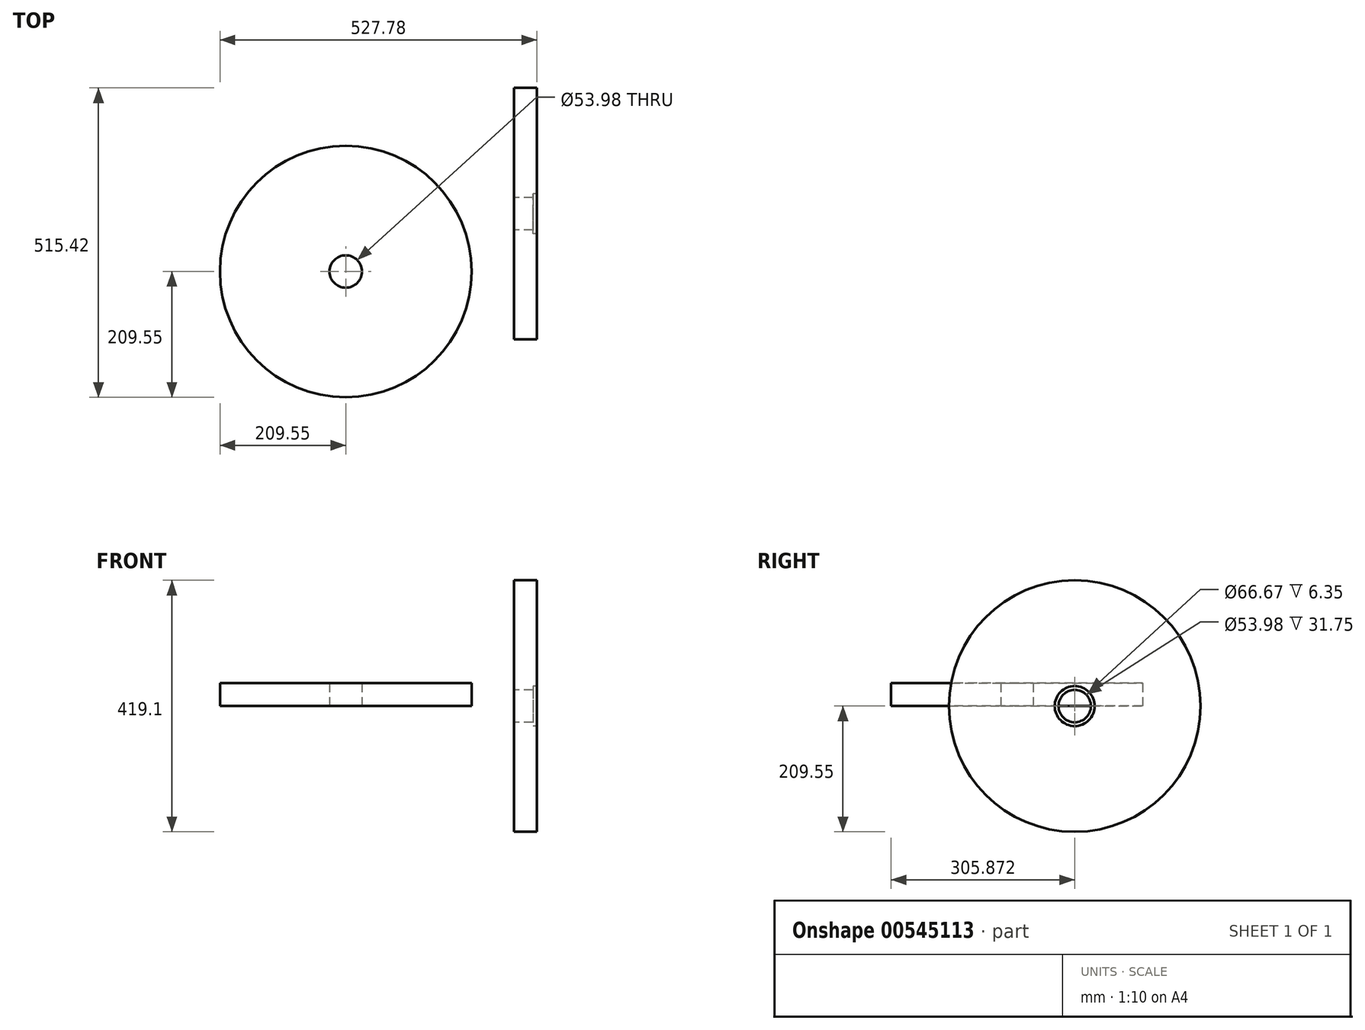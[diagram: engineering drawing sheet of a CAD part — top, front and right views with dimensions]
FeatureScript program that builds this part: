
annotation { "Feature Type Name" : "Feature", "Feature Type Description" : "" }
export const myFeature = defineFeature(function(context is Context, id is Id, definition is map)
    precondition{}
    {
        {
            var Q0;
            Q0=qCreatedBy(makeId("Top.planeOp"),FACE);
            var sketch = newSketch(context, id + "F0", { "sketchPlane" : qUnion([Q0])});
            skCircle(sketch, "E0", {"center": v(0, 0) * mm, "radius": 209.55 * mm});
            skCircle(sketch, "E1", {"center": v(0, 0) * mm, "radius": 26.99 * mm});
            skSolve(sketch);
        }
        {
            var Q0;
            Q0=makeQuery(id+"F0.imprint","IMPRINT",FACE,{"disambiguationData":[TD([[makeQuery(id+"F0.imprint","IMPRINT",EDGE,{"derivedFrom":sQuery(id+"F0.wireOp",EDGE,"E0")}),1.0]])]});
            extrude(context, id + "F1", {"entities" : qUnion([Q0]), "depth" : 38.1 * mm, "offsetDistance" : 25.4 * mm});
        }
        {
            var Q0;
            Q0=qCreatedBy(makeId("Top.planeOp"),FACE);
            var sketch = newSketch(context, id + "F2", { "sketchPlane" : qUnion([Q0])});
            skLineSegment(sketch, "E2", {"start": v(238.22, 96.32) * mm, "end": v(381.62, 96.32) * mm});
            skLineSegment(sketch, "E3", {"start": v(280.13, 123.3) * mm, "end": v(280.13, 276.4) * mm});
            skLineSegment(sketch, "E4", {"start": v(318.23, 276.4) * mm, "end": v(318.23, 129.66) * mm});
            skLineSegment(sketch, "E5", {"start": v(318.23, 129.66) * mm, "end": v(311.88, 129.66) * mm});
            skLineSegment(sketch, "E6", {"start": v(311.88, 129.66) * mm, "end": v(311.88, 123.3) * mm});
            skLineSegment(sketch, "E7", {"start": v(311.88, 123.3) * mm, "end": v(280.13, 123.3) * mm});
            skLineSegment(sketch, "E8", {"start": v(280.13, 305.87) * mm, "end": v(318.23, 305.87) * mm});
            skLineSegment(sketch, "E9", {"start": v(280.13, 276.4) * mm, "end": v(280.13, 305.87) * mm});
            skLineSegment(sketch, "E10", {"start": v(318.23, 305.87) * mm, "end": v(318.23, 276.4) * mm});
            skPoint(sketch, "E11.orphan", {"position": v(351.72, 305.87) * mm});
            skSolve(sketch);
        }
        {
            var Q0;
            Q0=makeQuery(id+"F2.imprint","IMPRINT",FACE,{"disambiguationData":[TD([[makeQuery(id+"F2.imprint","IMPRINT",EDGE,{"derivedFrom":sQuery(id+"F2.wireOp",EDGE,"E3")}),-1.0]])]});
            var Q1;
            Q1=sQuery(id+"F2.wireOp",EDGE,"E2");
            revolve(context, id + "F3", {"surfaceOperationType" : NewSurfaceOperationType.NEW, "entities" : qUnion([Q0]), "axis" : qUnion([Q1]), "revolveType" : RevolveType.FULL});
        }
    });
